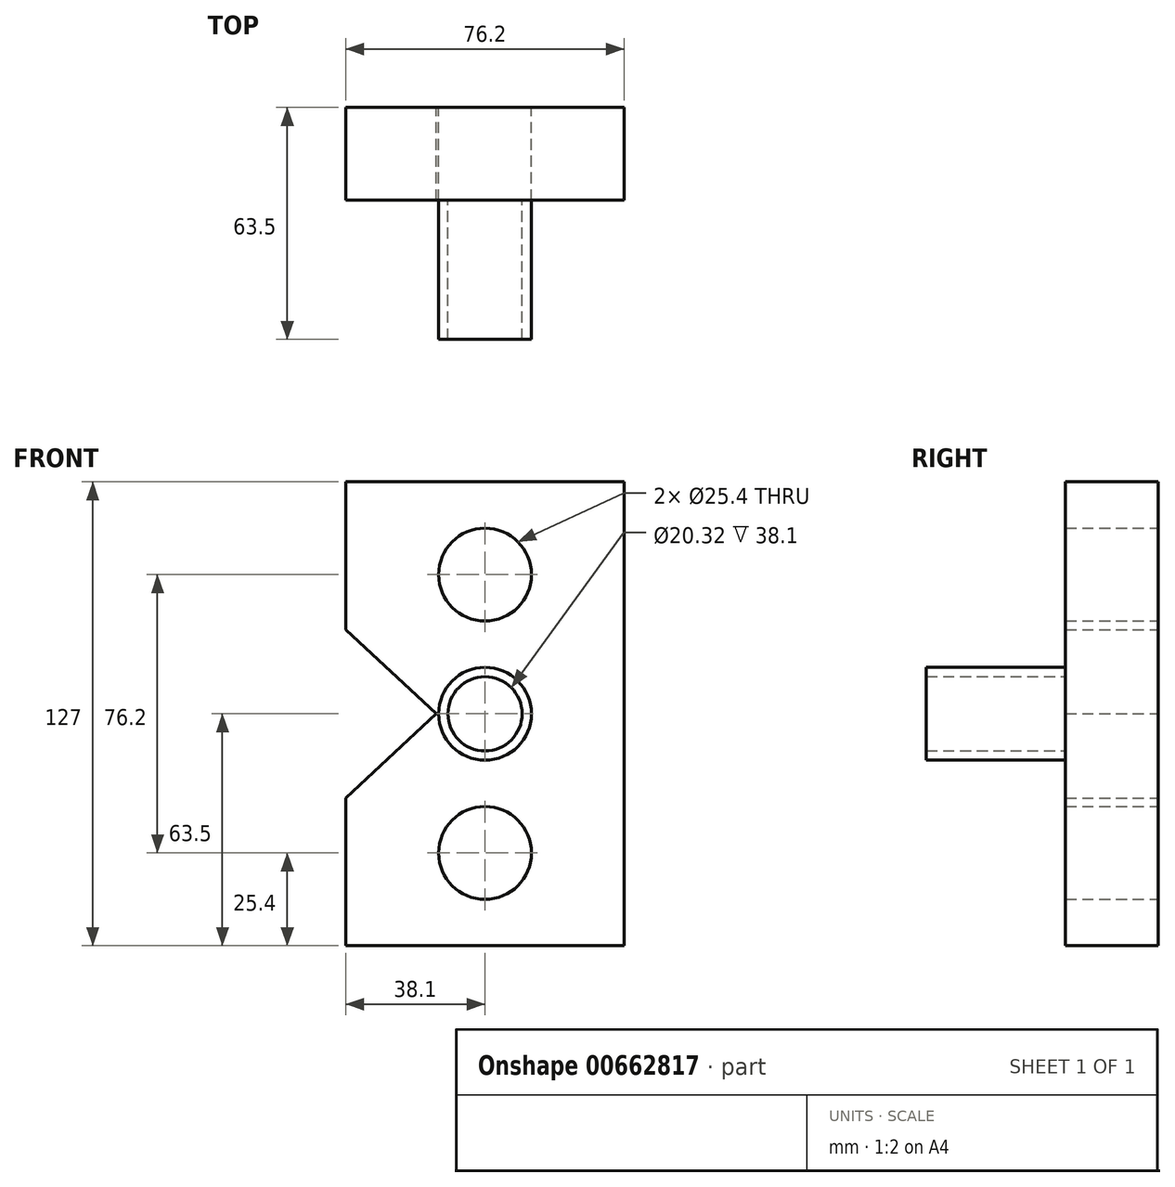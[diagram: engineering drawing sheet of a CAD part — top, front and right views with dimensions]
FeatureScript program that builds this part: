
annotation { "Feature Type Name" : "Feature", "Feature Type Description" : "" }
export const myFeature = defineFeature(function(context is Context, id is Id, definition is map)
    precondition{}
    {
        {
            var Q0;
            Q0=qCreatedBy(makeId("Front.planeOp"),FACE);
            var sketch = newSketch(context, id + "F0", { "sketchPlane" : qUnion([Q0])});
            skLineSegment(sketch, "E0.bottom", {"start": v(-38.1, 63.5) * mm, "end": v(38.1, 63.5) * mm});
            skLineSegment(sketch, "E0.top", {"start": v(-38.1, -63.5) * mm, "end": v(38.1, -63.5) * mm});
            skLineSegment(sketch, "E0.left", {"start": v(-38.1, 63.5) * mm, "end": v(-38.1, -63.5) * mm});
            skLineSegment(sketch, "E0.right", {"start": v(38.1, 63.5) * mm, "end": v(38.1, -63.5) * mm});
            skPoint(sketch, "E0.middle", {"position": v(0, 0) * mm});
            skCircle(sketch, "E1", {"center": v(0, 38.1) * mm, "radius": 12.7 * mm});
            skCircle(sketch, "E2", {"center": v(0, -38.1) * mm, "radius": 12.7 * mm});
            skLineSegment(sketch, "E3", {"start": v(-38.1, 23.04) * mm, "end": v(-13.33, 0) * mm});
            skLineSegment(sketch, "E4", {"start": v(-13.33, 0) * mm, "end": v(-38.1, -23.04) * mm});
            skSolve(sketch);
        }
        {
            var Q0;
            {var subQ3=sQuery(id+"F0.wireOp",EDGE,"E0.bottom");Q0=makeQuery(id+"F0.imprint","IMPRINT",FACE,{"disambiguationData":[TD([[makeQuery(id+"F0.imprint","IMPRINT",EDGE,{"derivedFrom":subQ3}),-1.0]])]});}
            extrude(context, id + "F1", {"entities" : qUnion([Q0]), "depth" : 25.4 * mm, "offsetDistance" : 25.4 * mm});
        }
        {
            var Q0;
            Q0=makeQuery(id+"F1.opExtrude","CAP_FACE",FACE,{"disambiguationData":[OSD([sQuery(id+"F0.wireOp",EDGE,"E0.bottom"),sQuery(id+"F0.wireOp",EDGE,"E0.top"),sQuery(id+"F0.wireOp",EDGE,"E0.left"),sQuery(id+"F0.wireOp",EDGE,"E0.right"),sQuery(id+"F0.wireOp",EDGE,"E1"),sQuery(id+"F0.wireOp",EDGE,"E2"),sQuery(id+"F0.wireOp",EDGE,"E3"),sQuery(id+"F0.wireOp",EDGE,"E4")])],"isStart":false});
            var sketch = newSketch(context, id + "F2", { "sketchPlane" : qUnion([Q0])});
            skCircle(sketch, "E5", {"center": v(0, 0) * mm, "radius": 12.7 * mm});
            skCircle(sketch, "E6", {"center": v(0, 0) * mm, "radius": 10.16 * mm});
            skSolve(sketch);
        }
        {
            var Q0;
            Q0 = qSketchRegion(id + "F2", true);
            extrude(context, id + "F3", {"entities" : qUnion([Q0]), "operationType" : NewBodyOperationType.ADD, "depth" : 38.1 * mm, "offsetDistance" : 25.4 * mm});
        }
    });
